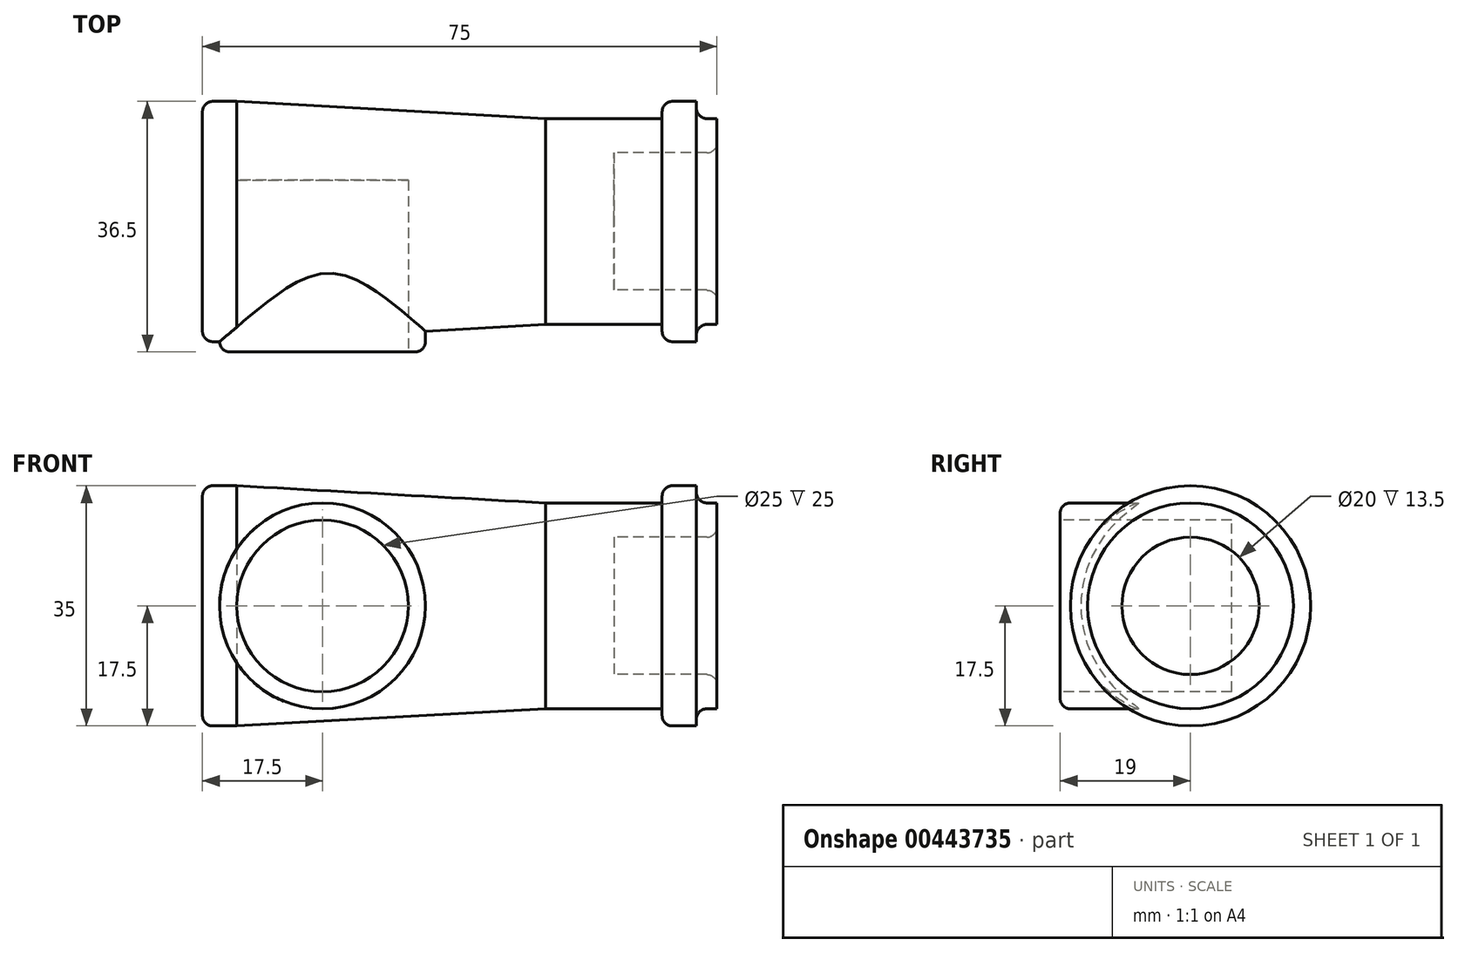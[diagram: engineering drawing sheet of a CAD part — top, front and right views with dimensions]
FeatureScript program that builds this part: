
annotation { "Feature Type Name" : "Feature", "Feature Type Description" : "" }
export const myFeature = defineFeature(function(context is Context, id is Id, definition is map)
    precondition{}
    {
        {
            var Q0;
            Q0=qCreatedBy(makeId("Front.planeOp"),FACE);
            var sketch = newSketch(context, id + "F0", { "sketchPlane" : qUnion([Q0])});
            skLineSegment(sketch, "E0", {"start": v(0, 0) * mm, "end": v(60, 0) * mm});
            skLineSegment(sketch, "E1", {"start": v(60, 0) * mm, "end": v(60, 10) * mm});
            skLineSegment(sketch, "E2", {"start": v(60, 10) * mm, "end": v(75, 10) * mm});
            skLineSegment(sketch, "E3", {"start": v(75, 10) * mm, "end": v(75, 15) * mm});
            skLineSegment(sketch, "E4", {"start": v(75, 15) * mm, "end": v(72, 15) * mm});
            skLineSegment(sketch, "E5", {"start": v(72, 15) * mm, "end": v(72, 17.5) * mm});
            skLineSegment(sketch, "E6", {"start": v(72, 17.5) * mm, "end": v(67, 17.5) * mm});
            skLineSegment(sketch, "E7", {"start": v(67, 17.5) * mm, "end": v(67, 15) * mm});
            skLineSegment(sketch, "E8", {"start": v(67, 15) * mm, "end": v(50, 15) * mm});
            skLineSegment(sketch, "E9", {"start": v(0, 17.5) * mm, "end": v(5, 17.5) * mm});
            skLineSegment(sketch, "E10", {"start": v(5, 17.5) * mm, "end": v(50, 15) * mm});
            skLineSegment(sketch, "E11", {"start": v(0, 17.5) * mm, "end": v(0, 0) * mm});
            skSolve(sketch);
        }
        {
            var Q0;
            Q0 = qSketchRegion(id + "F0", true);
            var Q1;
            Q1=makeQuery(id+"F0.imprint","IMPRINT",FACE,{"disambiguationData":[TD([[makeQuery(id+"F0.imprint","IMPRINT",EDGE,{"derivedFrom":sQuery(id+"F0.wireOp",EDGE,"E0")}),1.0]])]});
            var Q2;
            Q2=sQuery(id+"F0.wireOp",EDGE,"E0");
            revolve(context, id + "F1", {"entities" : qUnion([Q0, Q1]), "axis" : qUnion([Q2]), "revolveType" : RevolveType.FULL});
        }
        {
            var Q0;
            Q0=qCreatedBy(makeId("Front.planeOp"),FACE);
            var sketch = newSketch(context, id + "F2", { "sketchPlane" : qUnion([Q0])});
            skCircle(sketch, "E12", {"center": v(17.5, 0) * mm, "radius": 15 * mm});
            skSolve(sketch);
        }
        {
            var Q0;
            Q0 = qSketchRegion(id + "F2", true);
            extrude(context, id + "F3", {"entities" : qUnion([Q0]), "operationType" : NewBodyOperationType.ADD, "depth" : 19 * mm});
        }
        {
            var Q0;
            Q0=makeQuery(id+"F3.opExtrude","CAP_FACE",FACE,{"disambiguationData":[OSD([sQuery(id+"F2.wireOp",EDGE,"E12")])],"isStart":false});
            var sketch = newSketch(context, id + "F4", { "sketchPlane" : qUnion([Q0])});
            skCircle(sketch, "E13", {"center": v(17.5, 0) * mm, "radius": 12.5 * mm});
            skSolve(sketch);
        }
        {
            var Q0;
            Q0=makeQuery(id+"F4.imprint","IMPRINT",FACE,{"disambiguationData":[TD([[makeQuery(id+"F4.imprint","IMPRINT",EDGE,{"derivedFrom":sQuery(id+"F4.wireOp",EDGE,"E13")}),1.0]])]});
            extrude(context, id + "F5", {"entities" : qUnion([Q0]), "operationType" : NewBodyOperationType.REMOVE, "oppositeDirection" : true, "depth" : 25 * mm});
        }
        {
            var Q0;
            Q0=makeQuery(id+"F3.opExtrude","CAP_EDGE",EDGE,{"disambiguationData":[OSD([sQuery(id+"F2.wireOp",EDGE,"E12")])],"isStart":false});
            var Q1;
            Q1=makeQuery(id+"F1.opRevolve","SWEPT_EDGE",EDGE,{"disambiguationData":[OSD([sQuery(id+"F0.wireOp",EDGE,"E9"),sQuery(id+"F0.wireOp",EDGE,"E11")])]});
            var Q2;
            Q2=makeQuery(id+"F1.opRevolve","SWEPT_EDGE",EDGE,{"disambiguationData":[OSD([sQuery(id+"F0.wireOp",EDGE,"E6"),sQuery(id+"F0.wireOp",EDGE,"E7")])]});
            var Q3;
            Q3=makeQuery(id+"F1.opRevolve","SWEPT_EDGE",EDGE,{"disambiguationData":[OSD([sQuery(id+"F0.wireOp",EDGE,"E2"),sQuery(id+"F0.wireOp",EDGE,"E3")])]});
            var Q4;
            Q4=makeQuery(id+"F1.opRevolve","SWEPT_EDGE",EDGE,{"disambiguationData":[OSD([sQuery(id+"F0.wireOp",EDGE,"E4"),sQuery(id+"F0.wireOp",EDGE,"E5")])]});
            fillet(context, id + "F6", {"entities" : qUnion([Q0, Q1, Q2, Q3, Q4]), "radius" : 1.5 * mm, "tangentPropagation" : true, "allowEdgeOverflow" : false});
        }
    });
